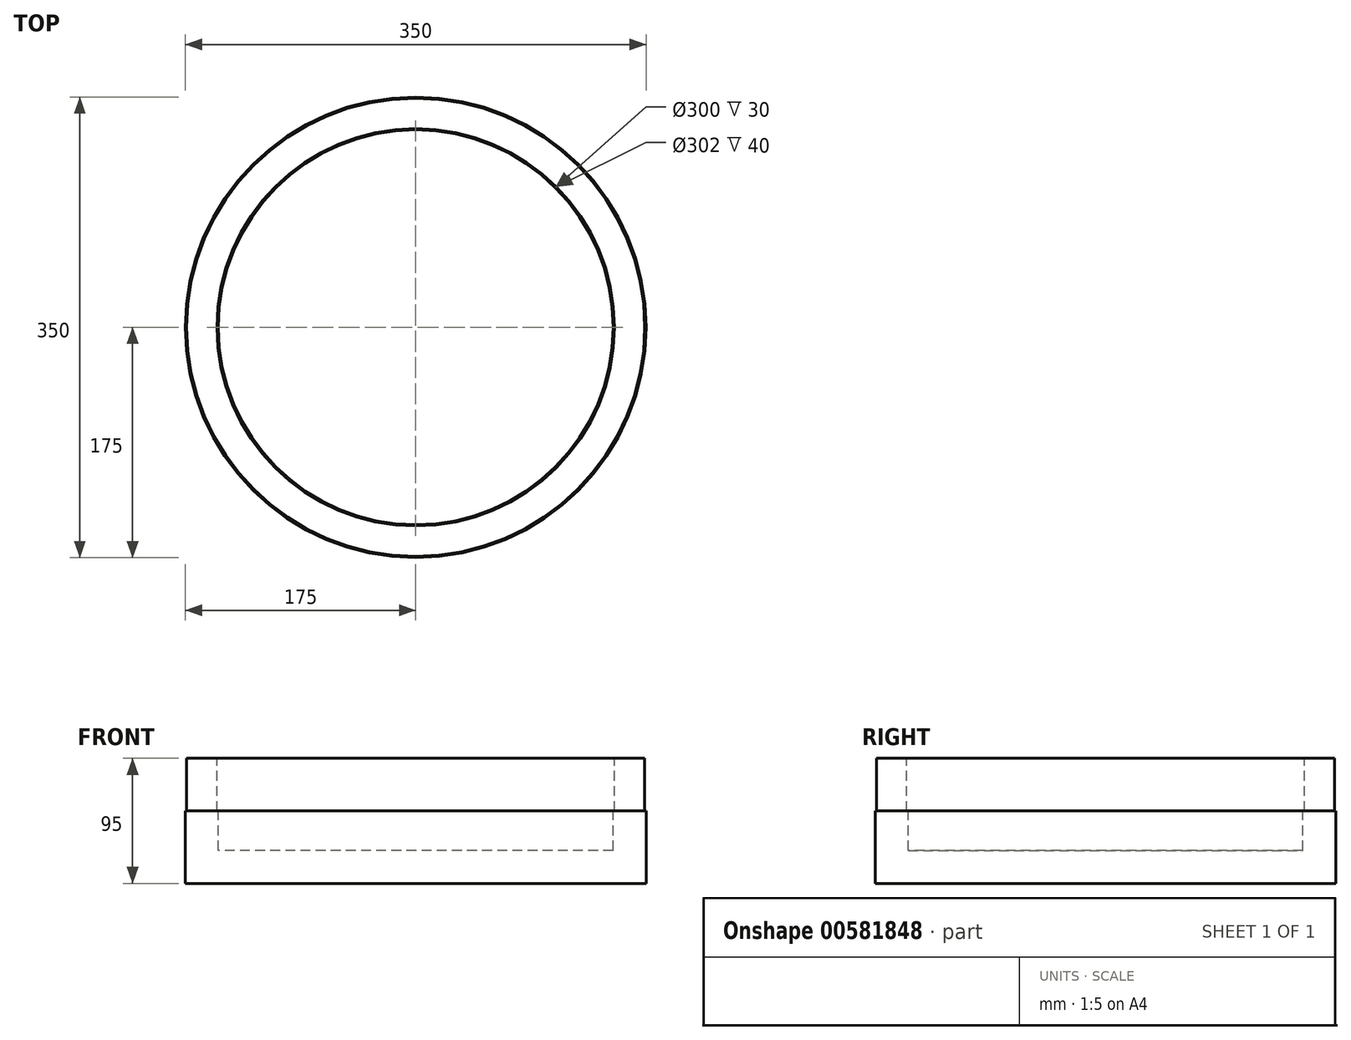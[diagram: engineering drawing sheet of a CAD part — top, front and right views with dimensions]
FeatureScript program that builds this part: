
annotation { "Feature Type Name" : "Feature", "Feature Type Description" : "" }
export const myFeature = defineFeature(function(context is Context, id is Id, definition is map)
    precondition{}
    {
        {
            var Q0;
            Q0=qCreatedBy(makeId("Front.planeOp"),FACE);
            var sketch = newSketch(context, id + "F0", { "sketchPlane" : qUnion([Q0])});
            skLineSegment(sketch, "E0", {"start": v(0, 136.7) * mm, "end": v(0, 0) * mm, "construction": true});
            skLineSegment(sketch, "E1", {"start": v(0, 0) * mm, "end": v(-175, 0) * mm});
            skLineSegment(sketch, "E2", {"start": v(-175, 0) * mm, "end": v(-175, 55) * mm});
            skLineSegment(sketch, "E3", {"start": v(-175, 55) * mm, "end": v(-174, 55) * mm});
            skLineSegment(sketch, "E4", {"start": v(-174, 55) * mm, "end": v(-174, 95) * mm});
            skLineSegment(sketch, "E5", {"start": v(-174, 95) * mm, "end": v(-151, 95) * mm});
            skLineSegment(sketch, "E6", {"start": v(-151, 95) * mm, "end": v(-151, 55) * mm});
            skLineSegment(sketch, "E7", {"start": v(-151, 55) * mm, "end": v(-150, 55) * mm});
            skLineSegment(sketch, "E8", {"start": v(-150, 55) * mm, "end": v(-150, 25) * mm});
            skLineSegment(sketch, "E9", {"start": v(-150, 25) * mm, "end": v(0, 25) * mm});
            skLineSegment(sketch, "E10", {"start": v(0, 25) * mm, "end": v(0, 0) * mm});
            skSolve(sketch);
        }
        {
            var Q0;
            Q0=qSketchRegion(id+"F0",true);
            var Q1;
            Q1=sQuery(id+"F0.wireOp",EDGE,"E0");
            revolve(context, id + "F1", {"surfaceOperationType" : NewSurfaceOperationType.NEW, "entities" : qUnion([Q0]), "axis" : qUnion([Q1]), "revolveType" : RevolveType.FULL});
        }
    });
